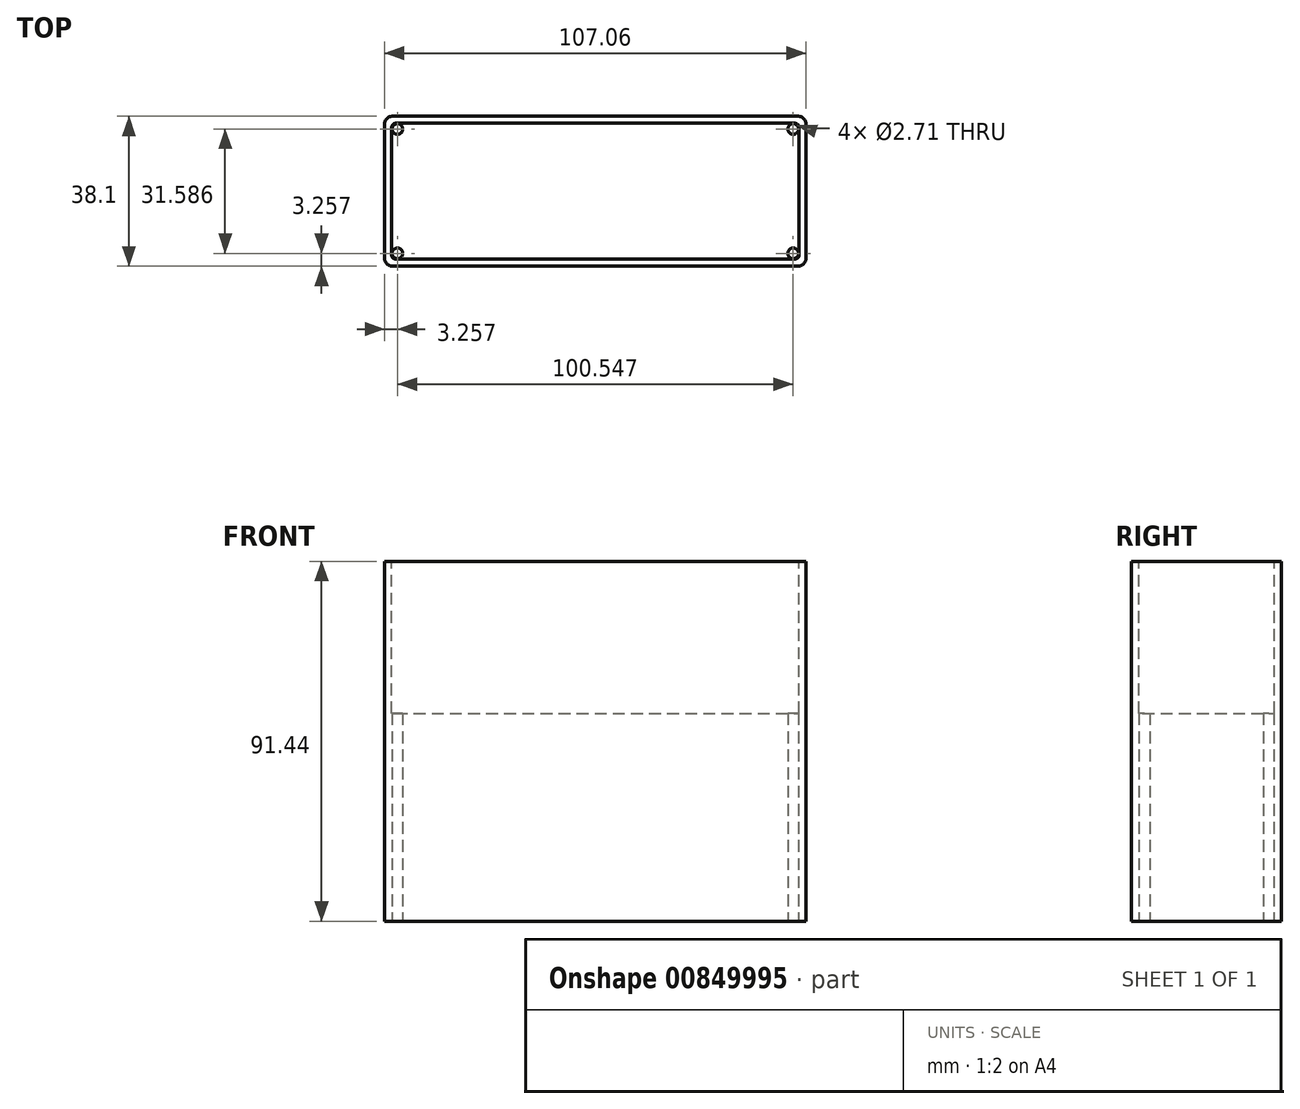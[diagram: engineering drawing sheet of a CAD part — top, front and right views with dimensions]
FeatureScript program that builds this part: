
annotation { "Feature Type Name" : "Feature", "Feature Type Description" : "" }
export const myFeature = defineFeature(function(context is Context, id is Id, definition is map)
    precondition{}
    {
        {
            var Q0;
            Q0=qCreatedBy(makeId("Top.planeOp"),FACE);
            var sketch = newSketch(context, id + "F0", { "sketchPlane" : qUnion([Q0])});
            skLineSegment(sketch, "E0.bottom", {"start": v(2, 0) * mm, "end": v(105.06, 0) * mm});
            skLineSegment(sketch, "E0.top", {"start": v(2, 38.1) * mm, "end": v(105.06, 38.1) * mm});
            skLineSegment(sketch, "E0.left", {"start": v(0, 2) * mm, "end": v(0, 36.1) * mm});
            skLineSegment(sketch, "E0.right", {"start": v(107.06, 2) * mm, "end": v(107.06, 36.1) * mm});
            skPoint(sketch, "E1.visualSharp", {"position": v(0, 38.1) * mm});
            skArc(sketch, "E1.filletArc", {"start": v(2, 38.1) * mm, "mid": v(0.59, 37.51) * mm, "end": v(0, 36.1) * mm});
            skPoint(sketch, "E2.visualSharp", {"position": v(107.06, 38.1) * mm});
            skArc(sketch, "E2.filletArc", {"start": v(107.06, 36.1) * mm, "mid": v(106.48, 37.51) * mm, "end": v(105.06, 38.1) * mm});
            skPoint(sketch, "E3.visualSharp", {"position": v(107.06, 0) * mm});
            skArc(sketch, "E3.filletArc", {"start": v(105.06, 0) * mm, "mid": v(106.48, 0.59) * mm, "end": v(107.06, 2) * mm});
            skPoint(sketch, "E4.visualSharp", {"position": v(0, 0) * mm});
            skArc(sketch, "E4.filletArc", {"start": v(0, 2) * mm, "mid": v(0.59, 0.59) * mm, "end": v(2, 0) * mm});
            skSolve(sketch);
        }
        {
            var Q0;
            Q0=qSketchRegion(id+"F0",true);
            var Q1;
            Q1=qSketchRegion(id+"F2",true);
            extrude(context, id + "F1", {"entities" : qUnion([Q0, Q1]), "depth" : 91.44 * mm, "offsetDistance" : 25 * mm});
        }
        {
            var Q0;
            Q0=makeQuery(id+"F1.opExtrude","CAP_FACE",FACE,{"disambiguationData":[OSD([sQuery(id+"F0.wireOp",EDGE,"E0.bottom"),sQuery(id+"F0.wireOp",EDGE,"E0.top"),sQuery(id+"F0.wireOp",EDGE,"E0.left"),sQuery(id+"F0.wireOp",EDGE,"E0.right"),sQuery(id+"F0.wireOp",EDGE,"E1.filletArc"),sQuery(id+"F0.wireOp",EDGE,"E2.filletArc"),sQuery(id+"F0.wireOp",EDGE,"E3.filletArc"),sQuery(id+"F0.wireOp",EDGE,"E4.filletArc")])],"isStart":false});
            var sketch = newSketch(context, id + "F2", { "sketchPlane" : qUnion([Q0])});
            skLineSegment(sketch, "E5.0", {"start": v(2, 38.1) * mm, "end": v(105.06, 38.1) * mm});
            skLineSegment(sketch, "E6.0", {"start": v(0, 2) * mm, "end": v(0, 36.1) * mm});
            skLineSegment(sketch, "E7.0", {"start": v(107.06, 2) * mm, "end": v(107.06, 36.1) * mm});
            skLineSegment(sketch, "E8.0", {"start": v(2, 0) * mm, "end": v(105.06, 0) * mm});
            skArc(sketch, "E9.0", {"start": v(2, 38.1) * mm, "mid": v(0.59, 37.51) * mm, "end": v(0, 36.1) * mm});
            skArc(sketch, "E10.0", {"start": v(107.06, 36.1) * mm, "mid": v(106.48, 37.51) * mm, "end": v(105.06, 38.1) * mm});
            skLineSegment(sketch, "E11.0", {"start": v(2.8, 36.3) * mm, "end": v(104.26, 36.3) * mm});
            skLineSegment(sketch, "E11.1", {"start": v(1.8, 2.8) * mm, "end": v(1.8, 35.3) * mm});
            skLineSegment(sketch, "E11.2", {"start": v(2.8, 1.8) * mm, "end": v(104.26, 1.8) * mm});
            skLineSegment(sketch, "E11.3", {"start": v(105.26, 2.8) * mm, "end": v(105.26, 35.3) * mm});
            skPoint(sketch, "E12.visualSharp", {"position": v(1.8, 36.3) * mm});
            skArc(sketch, "E12.filletArc", {"start": v(2.8, 36.3) * mm, "mid": v(2.1, 36) * mm, "end": v(1.8, 35.3) * mm});
            skPoint(sketch, "E13.visualSharp", {"position": v(1.8, 1.8) * mm});
            skArc(sketch, "E13.filletArc", {"start": v(1.8, 2.8) * mm, "mid": v(2.1, 2.1) * mm, "end": v(2.8, 1.8) * mm});
            skPoint(sketch, "E14.visualSharp", {"position": v(105.26, 1.8) * mm});
            skArc(sketch, "E14.filletArc", {"start": v(104.26, 1.8) * mm, "mid": v(104.97, 2.1) * mm, "end": v(105.26, 2.8) * mm});
            skPoint(sketch, "E15.visualSharp", {"position": v(105.26, 36.3) * mm});
            skArc(sketch, "E15.filletArc", {"start": v(105.26, 35.3) * mm, "mid": v(104.97, 36) * mm, "end": v(104.26, 36.3) * mm});
            skSolve(sketch);
        }
        {
            var Q0;
            Q0=qSketchRegion(id+"F2",true);
            extrude(context, id + "F3", {"entities" : qUnion([Q0]), "operationType" : NewBodyOperationType.REMOVE, "oppositeDirection" : true, "depth" : 38.6 * mm, "offsetDistance" : 25.4 * mm});
        }
        {
            var Q0;
            Q0=makeQuery(id+"F1.opExtrude","CAP_FACE",FACE,{"disambiguationData":[OSD([sQuery(id+"F0.wireOp",EDGE,"E0.bottom"),sQuery(id+"F0.wireOp",EDGE,"E0.top"),sQuery(id+"F0.wireOp",EDGE,"E0.left"),sQuery(id+"F0.wireOp",EDGE,"E0.right"),sQuery(id+"F0.wireOp",EDGE,"E1.filletArc"),sQuery(id+"F0.wireOp",EDGE,"E2.filletArc"),sQuery(id+"F0.wireOp",EDGE,"E3.filletArc"),sQuery(id+"F0.wireOp",EDGE,"E4.filletArc")])],"isStart":true});
            var sketch = newSketch(context, id + "F4", { "sketchPlane" : qUnion([Q0])});
            skArc(sketch, "E16.0", {"start": v(105.06, 0) * mm, "mid": v(106.48, -0.59) * mm, "end": v(107.06, -2) * mm});
            skArc(sketch, "E17", {"start": v(105.06, -5.8) * mm, "mid": v(102.37, -4.7) * mm, "end": v(101.25, -2) * mm});
            skLineSegment(sketch, "E18", {"start": v(105.06, -5.81) * mm, "end": v(107.06, -5.81) * mm});
            skLineSegment(sketch, "E19", {"start": v(107.06, -5.81) * mm, "end": v(107.06, -2) * mm});
            skLineSegment(sketch, "E20", {"start": v(101.25, -2) * mm, "end": v(101.25, 0) * mm});
            skLineSegment(sketch, "E21", {"start": v(101.25, 0) * mm, "end": v(105.06, 0) * mm});
            skLineSegment(sketch, "E22", {"start": v(53.53, -38.1) * mm, "end": v(53.53, 0) * mm, "construction": true});
            skLineSegment(sketch, "E23", {"start": v(107.06, -19.05) * mm, "end": v(0, -19.05) * mm, "construction": true});
            skLineSegment(sketch, "E24.MirrorCS", {"start": v(101.25, -38.1) * mm, "end": v(105.06, -38.1) * mm});
            skLineSegment(sketch, "E25.MirrorCS", {"start": v(101.25, -36.1) * mm, "end": v(101.25, -38.1) * mm});
            skLineSegment(sketch, "E26.MirrorCS", {"start": v(105.06, -32.3) * mm, "end": v(107.06, -32.3) * mm});
            skLineSegment(sketch, "E27.MirrorCS", {"start": v(107.06, -32.29) * mm, "end": v(107.06, -36.1) * mm});
            skArc(sketch, "E28.MirrorCS", {"start": v(105.06, -32.3) * mm, "mid": v(102.37, -33.4) * mm, "end": v(101.25, -36.1) * mm});
            skArc(sketch, "E29.MirrorCS", {"start": v(105.06, -38.1) * mm, "mid": v(106.48, -37.51) * mm, "end": v(107.06, -36.1) * mm});
            skArc(sketch, "E30.MirrorCS", {"start": v(2, -32.3) * mm, "mid": v(4.7, -33.4) * mm, "end": v(5.8, -36.1) * mm});
            skLineSegment(sketch, "E31.MirrorCS", {"start": v(0, -32.3) * mm, "end": v(0, -36.1) * mm});
            skLineSegment(sketch, "E32.MirrorCS", {"start": v(2, -32.3) * mm, "end": v(0, -32.3) * mm});
            skLineSegment(sketch, "E33.MirrorCS", {"start": v(5.81, -36.1) * mm, "end": v(5.81, -38.1) * mm});
            skLineSegment(sketch, "E34.MirrorCS", {"start": v(5.81, -38.1) * mm, "end": v(2, -38.1) * mm});
            skArc(sketch, "E35.MirrorCS", {"start": v(2, -38.1) * mm, "mid": v(0.59, -37.51) * mm, "end": v(0, -36.1) * mm});
            skArc(sketch, "E36.MirrorCS", {"start": v(2, 0) * mm, "mid": v(0.59, -0.59) * mm, "end": v(0, -2) * mm});
            skArc(sketch, "E37.MirrorCS", {"start": v(2, -5.8) * mm, "mid": v(4.7, -4.7) * mm, "end": v(5.8, -2) * mm});
            skLineSegment(sketch, "E38.MirrorCS", {"start": v(2, -5.81) * mm, "end": v(0, -5.81) * mm});
            skLineSegment(sketch, "E39.MirrorCS", {"start": v(0, -5.81) * mm, "end": v(0, -2) * mm});
            skLineSegment(sketch, "E40.MirrorCS", {"start": v(5.81, 0) * mm, "end": v(2, 0) * mm});
            skLineSegment(sketch, "E41.MirrorCS", {"start": v(5.8, -2) * mm, "end": v(5.8, 0) * mm});
            skSolve(sketch);
        }
        {
            var Q0;
            Q0=qSketchRegion(id+"F4",true);
            extrude(context, id + "F5", {"entities" : qUnion([Q0]), "operationType" : NewBodyOperationType.ADD, "oppositeDirection" : true, "depth" : 4.78 * mm, "offsetDistance" : 25.4 * mm});
        }
        {
            var Q0;
            Q0=makeQuery(id+"F1.opExtrude","CAP_FACE",FACE,{"disambiguationData":[OSD([sQuery(id+"F0.wireOp",EDGE,"E0.bottom"),sQuery(id+"F0.wireOp",EDGE,"E0.top"),sQuery(id+"F0.wireOp",EDGE,"E0.left"),sQuery(id+"F0.wireOp",EDGE,"E0.right"),sQuery(id+"F0.wireOp",EDGE,"E1.filletArc"),sQuery(id+"F0.wireOp",EDGE,"E2.filletArc"),sQuery(id+"F0.wireOp",EDGE,"E3.filletArc"),sQuery(id+"F0.wireOp",EDGE,"E4.filletArc")])],"isStart":true});
            var sketch = newSketch(context, id + "F6", { "sketchPlane" : qUnion([Q0])});
            skCircle(sketch, "E42", {"center": v(103.8, -3.26) * mm, "radius": 1.35 * mm});
            skLineSegment(sketch, "E43", {"start": v(106.48, -0.59) * mm, "end": v(102.37, -4.7) * mm, "construction": true});
            skCircle(sketch, "E44.MirrorC", {"center": v(3.26, -3.26) * mm, "radius": 1.35 * mm});
            skCircle(sketch, "E45.MirrorC", {"center": v(3.26, -34.84) * mm, "radius": 1.35 * mm});
            skCircle(sketch, "E46.MirrorC", {"center": v(103.8, -34.84) * mm, "radius": 1.35 * mm});
            skSolve(sketch);
        }
        {
            var Q0;
            Q0=qSketchRegion(id+"F6",true);
            extrude(context, id + "F7", {"entities" : qUnion([Q0]), "operationType" : NewBodyOperationType.REMOVE, "endBound" : BoundingType.UP_TO_NEXT, "oppositeDirection" : true, "depth" : 5.08 * mm, "offsetDistance" : 25.4 * mm});
        }
    });
